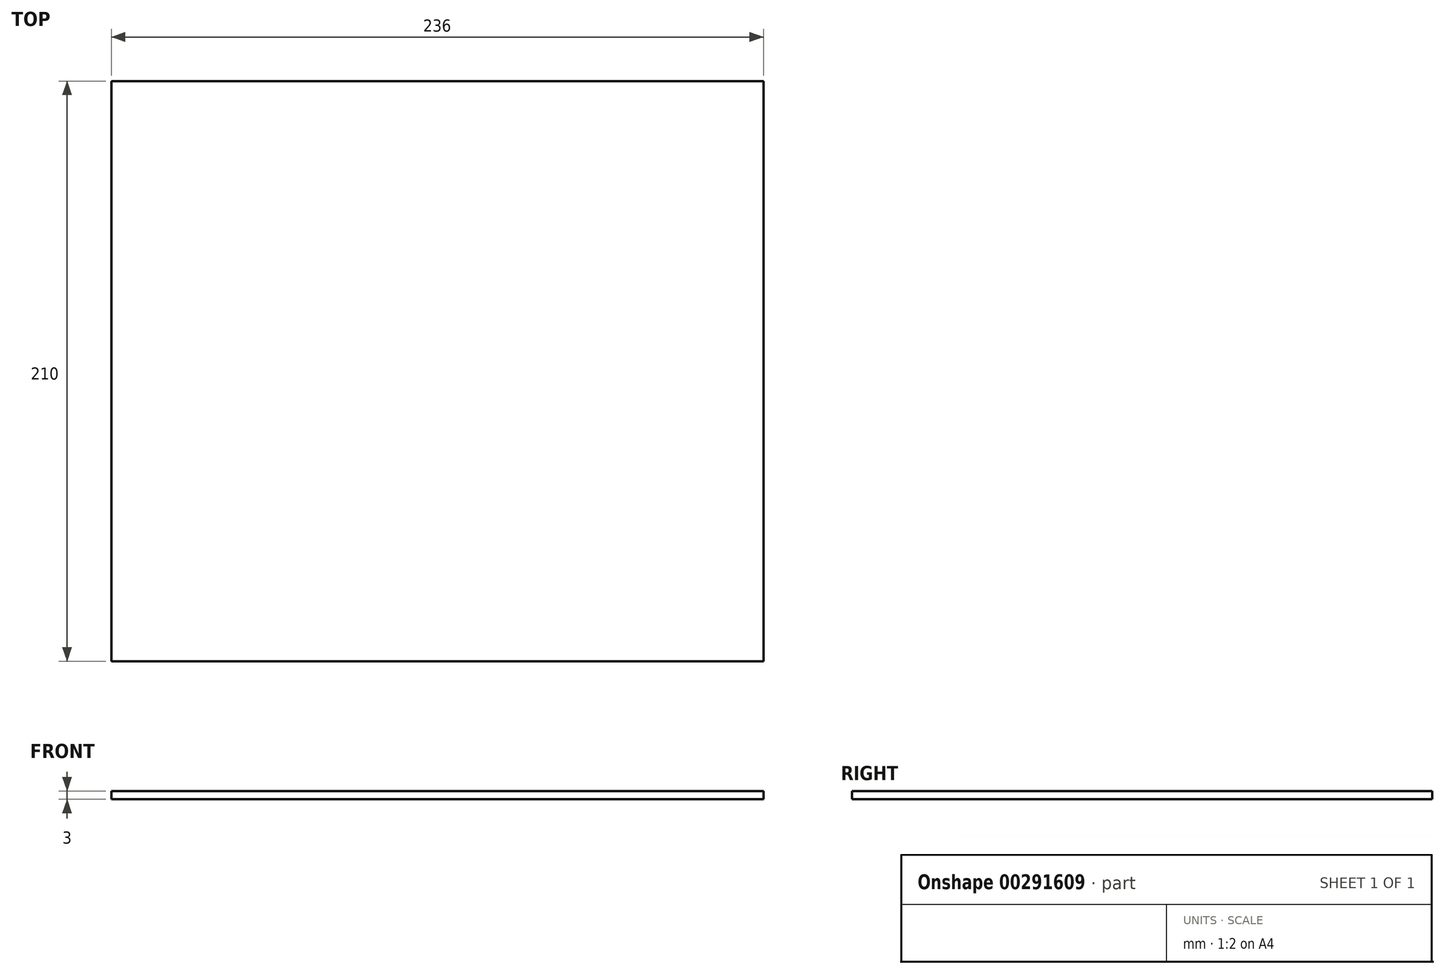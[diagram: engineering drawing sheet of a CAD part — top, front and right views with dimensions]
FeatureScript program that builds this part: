
annotation { "Feature Type Name" : "Feature", "Feature Type Description" : "" }
export const myFeature = defineFeature(function(context is Context, id is Id, definition is map)
    precondition{}
    {
        {
            var Q0;
            Q0=qCreatedBy(makeId("Top.planeOp"),FACE);
            var sketch = newSketch(context, id + "F0", { "sketchPlane" : qUnion([Q0])});
            skLineSegment(sketch, "E0.bottom", {"start": v(118, -105) * mm, "end": v(-118, -105) * mm});
            skLineSegment(sketch, "E0.top", {"start": v(118, 105) * mm, "end": v(-118, 105) * mm});
            skLineSegment(sketch, "E0.left", {"start": v(118, -105) * mm, "end": v(118, 105) * mm});
            skLineSegment(sketch, "E0.right", {"start": v(-118, -105) * mm, "end": v(-118, 105) * mm});
            skPoint(sketch, "E0.middle", {"position": v(0, 0) * mm});
            skSolve(sketch);
        }
        {
            var Q0;
            Q0 = qSketchRegion(id + "F0", true);
            extrude(context, id + "F1", {"entities" : qUnion([Q0]), "depth" : 3 * mm});
        }
    });
